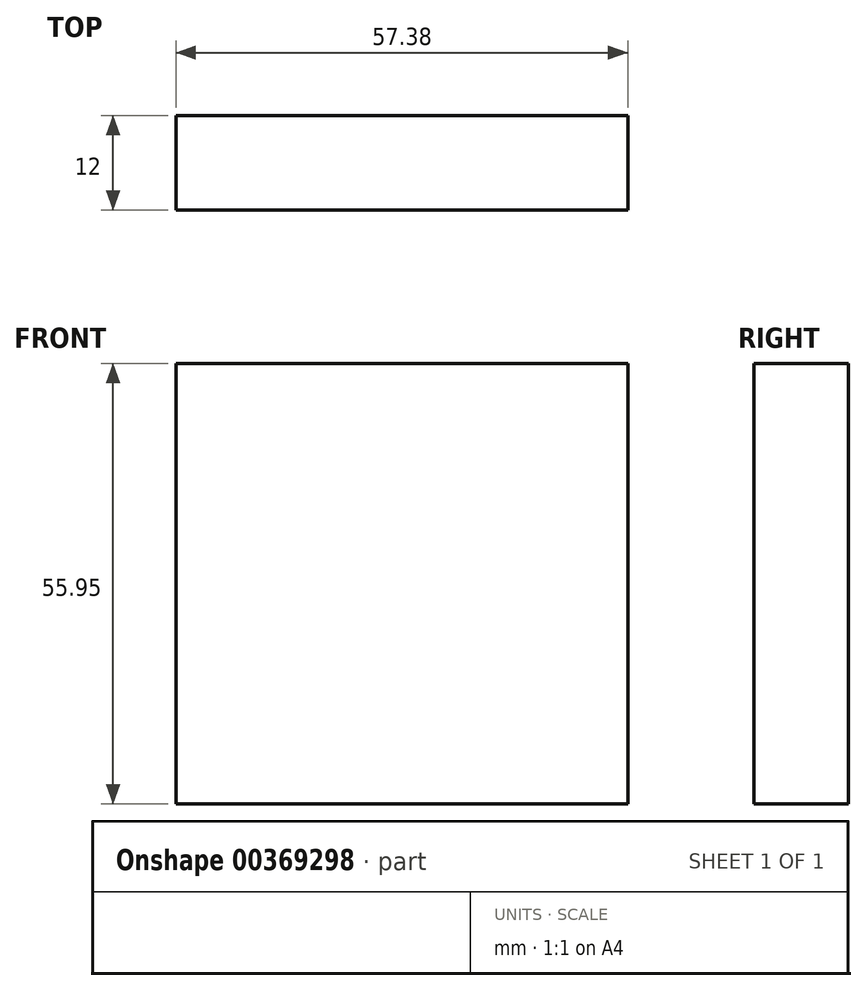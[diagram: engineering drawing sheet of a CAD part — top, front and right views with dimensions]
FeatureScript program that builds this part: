
annotation { "Feature Type Name" : "Feature", "Feature Type Description" : "" }
export const myFeature = defineFeature(function(context is Context, id is Id, definition is map)
    precondition{}
    {
        {
            var Q0;
            Q0=qCreatedBy(makeId("Front.planeOp"),FACE);
            var sketch = newSketch(context, id + "F0", { "sketchPlane" : qUnion([Q0])});
            skLineSegment(sketch, "E0.bottom", {"start": v(-30.24, -37.24) * mm, "end": v(27.14, -37.24) * mm});
            skLineSegment(sketch, "E0.top", {"start": v(-30.24, 18.71) * mm, "end": v(27.14, 18.71) * mm});
            skLineSegment(sketch, "E0.left", {"start": v(-30.24, -37.24) * mm, "end": v(-30.24, 18.71) * mm});
            skLineSegment(sketch, "E0.right", {"start": v(27.14, -37.24) * mm, "end": v(27.14, 18.71) * mm});
            skSolve(sketch);
        }
        {
            var Q0;
            Q0 = qSketchRegion(id + "F0", true);
            extrude(context, id + "F1", {"entities" : qUnion([Q0]), "depth" : 12 * mm});
        }
    });
